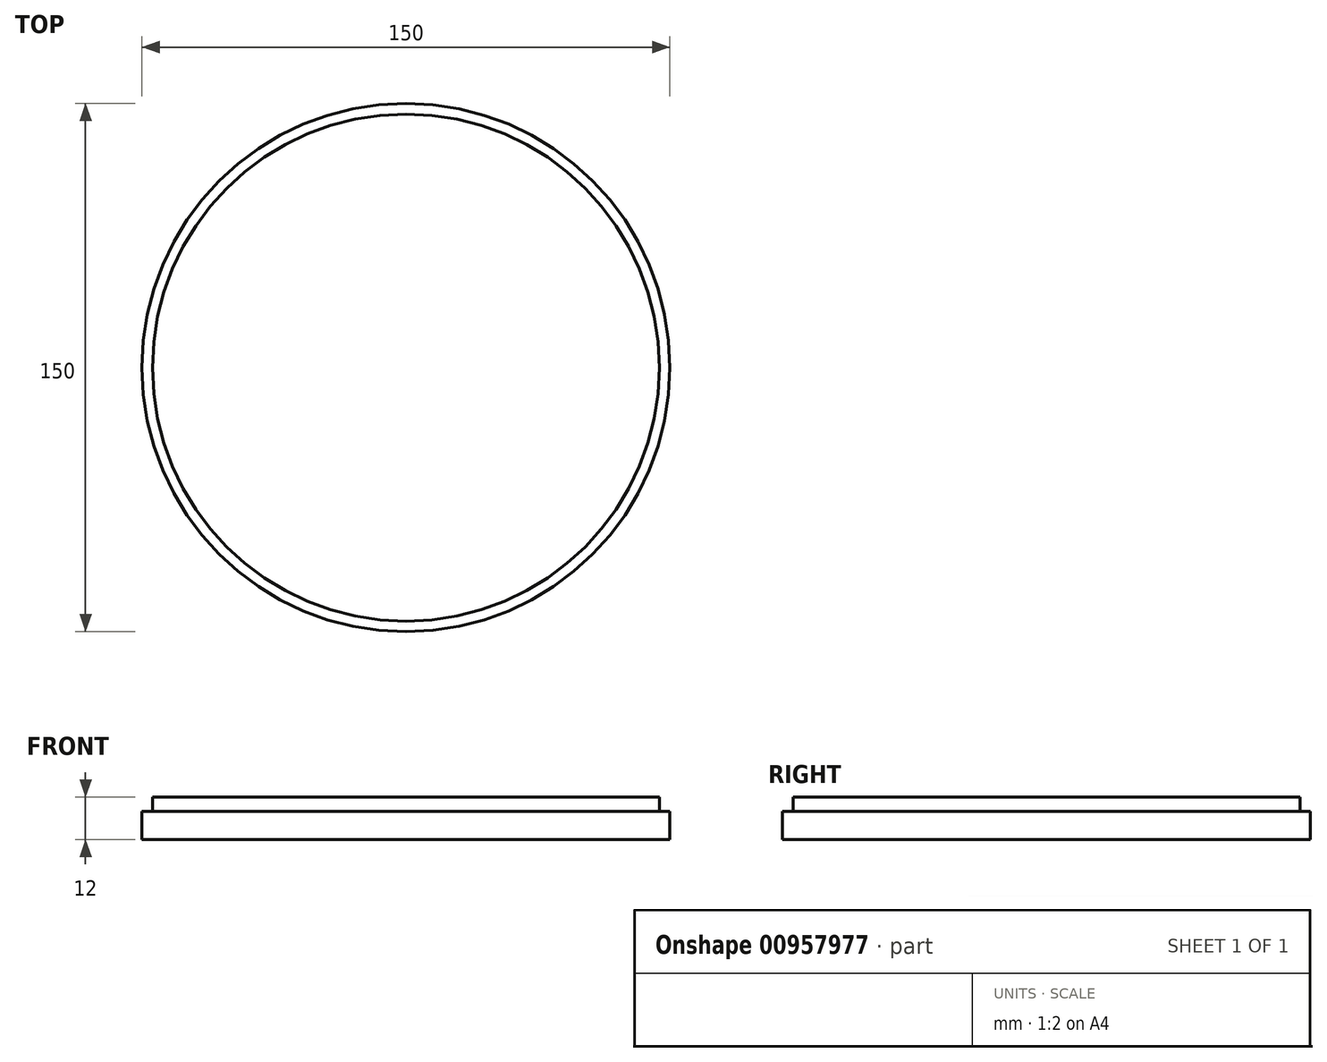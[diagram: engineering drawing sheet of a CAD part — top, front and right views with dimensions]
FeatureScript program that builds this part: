
annotation { "Feature Type Name" : "Feature", "Feature Type Description" : "" }
export const myFeature = defineFeature(function(context is Context, id is Id, definition is map)
    precondition{}
    {
        {
            var Q0;
            Q0=qCreatedBy(makeId("Top.planeOp"),FACE);
            var sketch = newSketch(context, id + "F0", { "sketchPlane" : qUnion([Q0])});
            skCircle(sketch, "E0", {"center": v(0, 0) * mm, "radius": 75 * mm});
            skSolve(sketch);
        }
        {
            assignVariable(context, id + "F1", {"name" : "baseThickness", "anyValue" : 12 * mm});
        }
        {
            var Q0;
            Q0=makeQuery(id+"F0.imprint","IMPRINT",FACE,{"disambiguationData":[TD([[makeQuery(id+"F0.imprint","IMPRINT",EDGE,{"derivedFrom":sQuery(id+"F0.wireOp",EDGE,"E0")}),1.0]])]});
            extrude(context, id + "F2", {"entities" : qUnion([Q0]), "depth" : getVariable(context, 'baseThickness'), "offsetDistance" : 25 * mm});
        }
        {
            var Q0;
            Q0=makeQuery(id+"F2.opExtrude","CAP_FACE",FACE,{"disambiguationData":[OSD([sQuery(id+"F0.wireOp",EDGE,"E0")])],"isStart":false});
            var sketch = newSketch(context, id + "F3", { "sketchPlane" : qUnion([Q0])});
            skCircle(sketch, "E1", {"center": v(0, 0) * mm, "radius": 72 * mm});
            skSolve(sketch);
        }
        {
            var Q0;
            Q0=makeQuery(id+"F3.imprint","IMPRINT",FACE,{"disambiguationData":[TD([[makeQuery(id+"F3.imprint","IMPRINT",EDGE,{"derivedFrom":sQuery(id+"F3.wireOp",EDGE,"E1")}),-1.0]])]});
            extrude(context, id + "F4", {"entities" : qUnion([Q0]), "operationType" : NewBodyOperationType.REMOVE, "oppositeDirection" : true, "depth" : 4 * mm, "offsetDistance" : 25 * mm});
        }
    });
